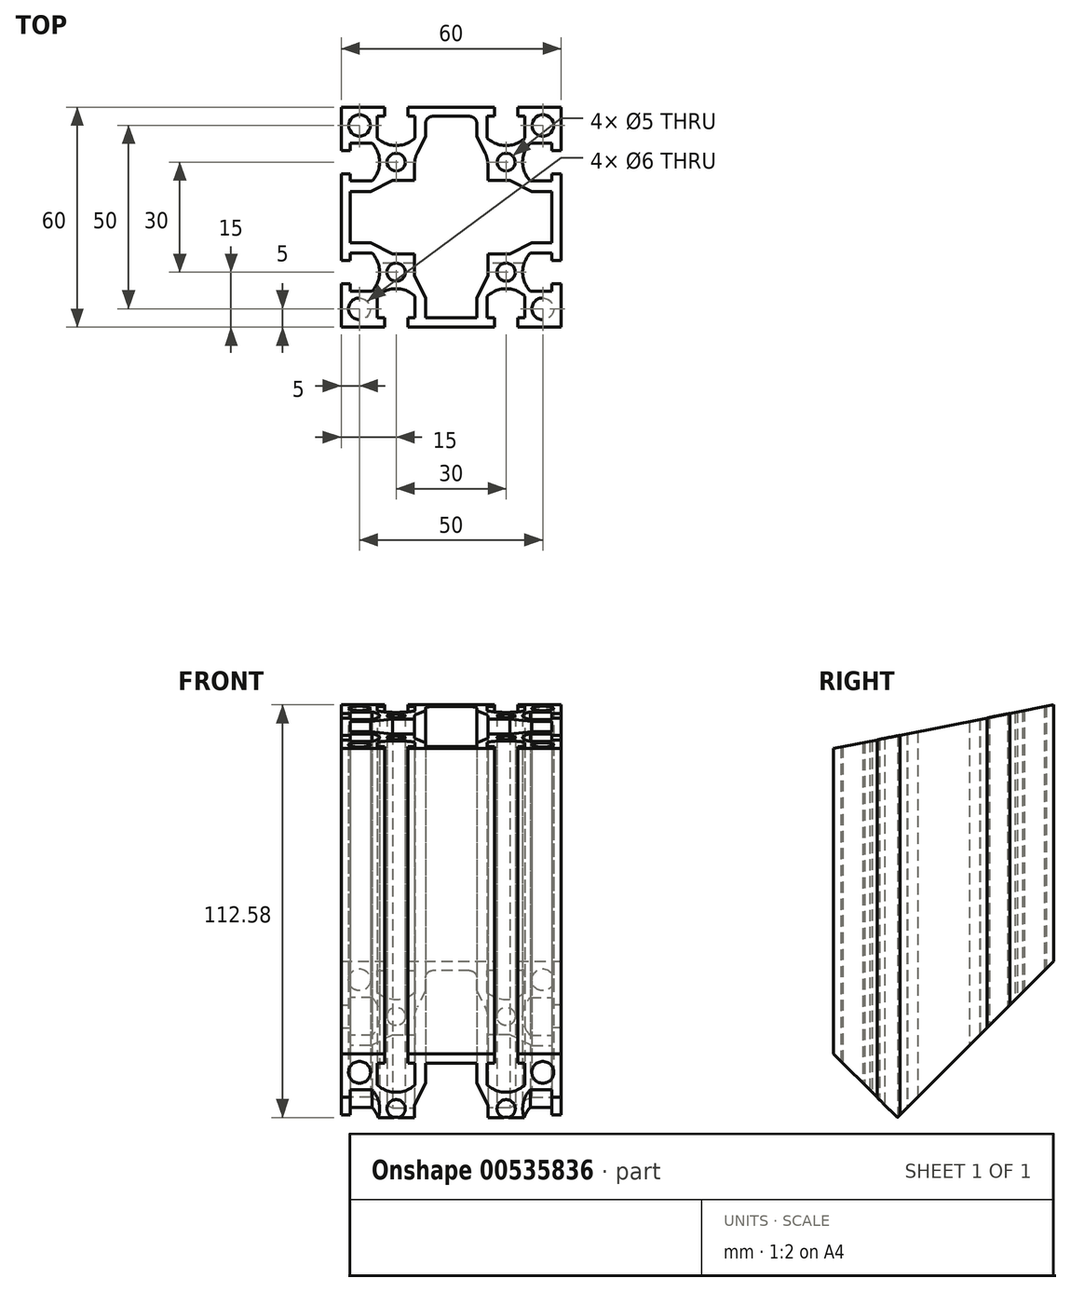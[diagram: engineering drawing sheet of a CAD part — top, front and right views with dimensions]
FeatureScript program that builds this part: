
annotation { "Feature Type Name" : "Feature", "Feature Type Description" : "" }
export const myFeature = defineFeature(function(context is Context, id is Id, definition is map)
    precondition{}
    {
        {
            var Q0;
            Q0=qCreatedBy(makeId("Top.planeOp"),FACE);
            var sketch = newSketch(context, id + "F0", { "sketchPlane" : qUnion([Q0])});
            skLineSegment(sketch, "E0.bottom", {"start": v(30, -30) * mm, "end": v(-30, -30) * mm});
            skLineSegment(sketch, "E0.top", {"start": v(30, 30) * mm, "end": v(-30, 30) * mm});
            skLineSegment(sketch, "E0.left", {"start": v(30, -30) * mm, "end": v(30, 30) * mm});
            skLineSegment(sketch, "E0.right", {"start": v(-30, -30) * mm, "end": v(-30, 30) * mm});
            skPoint(sketch, "E0.middle", {"position": v(0, 0) * mm});
            skLineSegment(sketch, "E1.top", {"start": v(-11.85, 30) * mm, "end": v(-18.15, 30) * mm});
            skLineSegment(sketch, "E1.left", {"start": v(-11.85, 27.5) * mm, "end": v(-11.85, 30) * mm});
            skLineSegment(sketch, "E1.right", {"start": v(-18.15, 27.5) * mm, "end": v(-18.15, 30) * mm});
            skPoint(sketch, "E1.middle", {"position": v(-15, 28.75) * mm});
            skLineSegment(sketch, "E2.bottom", {"start": v(-9.85, 27.5) * mm, "end": v(-11.85, 27.5) * mm});
            skLineSegment(sketch, "E2.left", {"start": v(-9.85, 27.5) * mm, "end": v(-9.85, 21.55) * mm});
            skLineSegment(sketch, "E2.right", {"start": v(-20.15, 27.5) * mm, "end": v(-20.15, 21.55) * mm});
            skPoint(sketch, "E2.middle", {"position": v(-15, 24.52) * mm});
            skArc(sketch, "E3", {"start": v(-20.15, 21.55) * mm, "mid": v(-15, 19.5) * mm, "end": v(-9.85, 21.55) * mm});
            skPoint(sketch, "E4.MirrorP", {"position": v(15, 24.52) * mm});
            skPoint(sketch, "E5.MirrorP", {"position": v(15, 28.75) * mm});
            skLineSegment(sketch, "E6.MirrorCS", {"start": v(11.85, 27.5) * mm, "end": v(11.85, 30) * mm});
            skLineSegment(sketch, "E7.MirrorCS", {"start": v(18.15, 27.5) * mm, "end": v(18.15, 30) * mm});
            skLineSegment(sketch, "E8.MirrorCS", {"start": v(9.85, 27.5) * mm, "end": v(11.85, 27.5) * mm});
            skLineSegment(sketch, "E9.MirrorCS", {"start": v(9.85, 27.5) * mm, "end": v(9.85, 21.55) * mm});
            skArc(sketch, "E10.MirrorCS", {"start": v(20.15, 21.55) * mm, "mid": v(15, 19.5) * mm, "end": v(9.85, 21.55) * mm});
            skLineSegment(sketch, "E11.MirrorCS", {"start": v(20.15, 27.5) * mm, "end": v(20.15, 21.55) * mm});
            skLineSegment(sketch, "E12.MirrorCS", {"start": v(11.85, 30) * mm, "end": v(18.15, 30) * mm});
            skLineSegment(sketch, "E13.1.0", {"start": v(27.5, 20.15) * mm, "end": v(21.55, 20.15) * mm});
            skLineSegment(sketch, "E13.1.1", {"start": v(27.5, 9.85) * mm, "end": v(21.55, 9.85) * mm});
            skArc(sketch, "E13.1.2", {"start": v(21.55, 20.15) * mm, "mid": v(19.5, 15) * mm, "end": v(21.55, 9.85) * mm});
            skLineSegment(sketch, "E13.1.3", {"start": v(27.5, -9.85) * mm, "end": v(21.55, -9.85) * mm});
            skLineSegment(sketch, "E13.1.4", {"start": v(27.5, -20.15) * mm, "end": v(21.55, -20.15) * mm});
            skPoint(sketch, "E13.1.5", {"position": v(28.75, 15) * mm});
            skPoint(sketch, "E13.1.6", {"position": v(28.75, -15) * mm});
            skArc(sketch, "E13.1.7", {"start": v(21.55, -20.15) * mm, "mid": v(19.5, -15) * mm, "end": v(21.55, -9.85) * mm});
            skPoint(sketch, "E13.1.8", {"position": v(24.52, -15) * mm});
            skPoint(sketch, "E13.1.9", {"position": v(24.52, 15) * mm});
            skLineSegment(sketch, "E13.1.10", {"start": v(27.5, 9.85) * mm, "end": v(27.5, 20.15) * mm});
            skLineSegment(sketch, "E13.1.11", {"start": v(27.5, -11.85) * mm, "end": v(27.5, -18.15) * mm});
            skLineSegment(sketch, "E13.1.12", {"start": v(30, 11.85) * mm, "end": v(30, 18.15) * mm});
            skLineSegment(sketch, "E13.1.13", {"start": v(30, -11.85) * mm, "end": v(30, -18.15) * mm});
            skLineSegment(sketch, "E13.1.14", {"start": v(27.5, 18.15) * mm, "end": v(30, 18.15) * mm});
            skLineSegment(sketch, "E13.1.15", {"start": v(27.5, 11.85) * mm, "end": v(30, 11.85) * mm});
            skLineSegment(sketch, "E13.1.16", {"start": v(27.5, 11.85) * mm, "end": v(27.5, 18.15) * mm});
            skLineSegment(sketch, "E13.1.17", {"start": v(27.5, -9.85) * mm, "end": v(27.5, -20.15) * mm});
            skLineSegment(sketch, "E13.1.18", {"start": v(27.5, -18.15) * mm, "end": v(30, -18.15) * mm});
            skLineSegment(sketch, "E13.1.19", {"start": v(27.5, -11.85) * mm, "end": v(30, -11.85) * mm});
            skLineSegment(sketch, "E13.2.0", {"start": v(20.15, -27.5) * mm, "end": v(20.15, -21.55) * mm});
            skLineSegment(sketch, "E13.2.1", {"start": v(9.85, -27.5) * mm, "end": v(9.85, -21.55) * mm});
            skArc(sketch, "E13.2.2", {"start": v(20.15, -21.55) * mm, "mid": v(15, -19.5) * mm, "end": v(9.85, -21.55) * mm});
            skLineSegment(sketch, "E13.2.3", {"start": v(-9.85, -27.5) * mm, "end": v(-9.85, -21.55) * mm});
            skLineSegment(sketch, "E13.2.4", {"start": v(-20.15, -27.5) * mm, "end": v(-20.15, -21.55) * mm});
            skPoint(sketch, "E13.2.5", {"position": v(15, -28.75) * mm});
            skPoint(sketch, "E13.2.6", {"position": v(-15, -28.75) * mm});
            skArc(sketch, "E13.2.7", {"start": v(-20.15, -21.55) * mm, "mid": v(-15, -19.5) * mm, "end": v(-9.85, -21.55) * mm});
            skPoint(sketch, "E13.2.8", {"position": v(-15, -24.52) * mm});
            skPoint(sketch, "E13.2.9", {"position": v(15, -24.52) * mm});
            skLineSegment(sketch, "E13.2.10", {"start": v(9.85, -27.5) * mm, "end": v(20.15, -27.5) * mm});
            skLineSegment(sketch, "E13.2.11", {"start": v(-11.85, -27.5) * mm, "end": v(-18.15, -27.5) * mm});
            skLineSegment(sketch, "E13.2.12", {"start": v(11.85, -30) * mm, "end": v(18.15, -30) * mm});
            skLineSegment(sketch, "E13.2.13", {"start": v(-11.85, -30) * mm, "end": v(-18.15, -30) * mm});
            skLineSegment(sketch, "E13.2.14", {"start": v(18.15, -27.5) * mm, "end": v(18.15, -30) * mm});
            skLineSegment(sketch, "E13.2.15", {"start": v(11.85, -27.5) * mm, "end": v(11.85, -30) * mm});
            skLineSegment(sketch, "E13.2.16", {"start": v(11.85, -27.5) * mm, "end": v(18.15, -27.5) * mm});
            skLineSegment(sketch, "E13.2.17", {"start": v(-9.85, -27.5) * mm, "end": v(-20.15, -27.5) * mm});
            skLineSegment(sketch, "E13.2.18", {"start": v(-18.15, -27.5) * mm, "end": v(-18.15, -30) * mm});
            skLineSegment(sketch, "E13.2.19", {"start": v(-11.85, -27.5) * mm, "end": v(-11.85, -30) * mm});
            skLineSegment(sketch, "E13.3.0", {"start": v(-27.5, -20.15) * mm, "end": v(-21.55, -20.15) * mm});
            skLineSegment(sketch, "E13.3.1", {"start": v(-27.5, -9.85) * mm, "end": v(-21.55, -9.85) * mm});
            skArc(sketch, "E13.3.2", {"start": v(-21.55, -20.15) * mm, "mid": v(-19.5, -15) * mm, "end": v(-21.55, -9.85) * mm});
            skLineSegment(sketch, "E13.3.3", {"start": v(-27.5, 9.85) * mm, "end": v(-21.55, 9.85) * mm});
            skLineSegment(sketch, "E13.3.4", {"start": v(-27.5, 20.15) * mm, "end": v(-21.55, 20.15) * mm});
            skPoint(sketch, "E13.3.5", {"position": v(-28.75, -15) * mm});
            skPoint(sketch, "E13.3.6", {"position": v(-28.75, 15) * mm});
            skArc(sketch, "E13.3.7", {"start": v(-21.55, 20.15) * mm, "mid": v(-19.5, 15) * mm, "end": v(-21.55, 9.85) * mm});
            skPoint(sketch, "E13.3.8", {"position": v(-24.52, 15) * mm});
            skPoint(sketch, "E13.3.9", {"position": v(-24.52, -15) * mm});
            skLineSegment(sketch, "E13.3.10", {"start": v(-27.5, -9.85) * mm, "end": v(-27.5, -20.15) * mm});
            skLineSegment(sketch, "E13.3.11", {"start": v(-27.5, 11.85) * mm, "end": v(-27.5, 18.15) * mm});
            skLineSegment(sketch, "E13.3.12", {"start": v(-30, -11.85) * mm, "end": v(-30, -18.15) * mm});
            skLineSegment(sketch, "E13.3.13", {"start": v(-30, 11.85) * mm, "end": v(-30, 18.15) * mm});
            skLineSegment(sketch, "E13.3.14", {"start": v(-27.5, -18.15) * mm, "end": v(-30, -18.15) * mm});
            skLineSegment(sketch, "E13.3.15", {"start": v(-27.5, -11.85) * mm, "end": v(-30, -11.85) * mm});
            skLineSegment(sketch, "E13.3.16", {"start": v(-27.5, -11.85) * mm, "end": v(-27.5, -18.15) * mm});
            skLineSegment(sketch, "E13.3.17", {"start": v(-27.5, 9.85) * mm, "end": v(-27.5, 20.15) * mm});
            skLineSegment(sketch, "E13.3.18", {"start": v(-27.5, 18.15) * mm, "end": v(-30, 18.15) * mm});
            skLineSegment(sketch, "E13.3.19", {"start": v(-27.5, 11.85) * mm, "end": v(-30, 11.85) * mm});
            skLineSegment(sketch, "E13.anchor1", {"start": v(0, 0) * mm, "end": v(-20.15, 21.55) * mm, "construction": true});
            skLineSegment(sketch, "E13.anchor2", {"start": v(0, 0) * mm, "end": v(-21.55, -20.15) * mm, "construction": true});
            skLineSegment(sketch, "E14.trimOffspring", {"start": v(-18.15, 27.5) * mm, "end": v(-20.15, 27.5) * mm});
            skLineSegment(sketch, "E15.trimOffspring", {"start": v(18.15, 27.5) * mm, "end": v(20.15, 27.5) * mm});
            skCircle(sketch, "E16", {"center": v(-15, 15) * mm, "radius": 2.5 * mm});
            skCircle(sketch, "E17", {"center": v(-25, 25) * mm, "radius": 3 * mm});
            skCircle(sketch, "E18.MirrorC", {"center": v(25, 25) * mm, "radius": 3 * mm});
            skCircle(sketch, "E19.MirrorC", {"center": v(25, -25) * mm, "radius": 3 * mm});
            skCircle(sketch, "E20.MirrorC", {"center": v(-25, -25) * mm, "radius": 3 * mm});
            skCircle(sketch, "E21.MirrorC", {"center": v(15, 15) * mm, "radius": 2.5 * mm});
            skCircle(sketch, "E22.MirrorC", {"center": v(15, -15) * mm, "radius": 2.5 * mm});
            skCircle(sketch, "E23.MirrorC", {"center": v(-15, -15) * mm, "radius": 2.5 * mm});
            skLineSegment(sketch, "E24", {"start": v(-7, 27.5) * mm, "end": v(0, 27.5) * mm});
            skLineSegment(sketch, "E25", {"start": v(-7, 27.5) * mm, "end": v(-7, 22) * mm});
            skLineSegment(sketch, "E26", {"start": v(-10, 10) * mm, "end": v(-10, 16) * mm});
            skLineSegment(sketch, "E27", {"start": v(-10, 16) * mm, "end": v(-7, 22) * mm});
            skLineSegment(sketch, "E28.MirrorCS", {"start": v(10, 10) * mm, "end": v(10, 16) * mm});
            skLineSegment(sketch, "E29.MirrorCS", {"start": v(10, 16) * mm, "end": v(7, 22) * mm});
            skLineSegment(sketch, "E30.MirrorCS", {"start": v(7, 27.5) * mm, "end": v(0, 27.5) * mm});
            skLineSegment(sketch, "E31.MirrorCS", {"start": v(7, 27.5) * mm, "end": v(7, 22) * mm});
            skLineSegment(sketch, "E32.1.0", {"start": v(-10, -10) * mm, "end": v(-16, -10) * mm});
            skLineSegment(sketch, "E32.1.1", {"start": v(-16, -10) * mm, "end": v(-22, -7) * mm});
            skLineSegment(sketch, "E32.1.2", {"start": v(-27.5, -7) * mm, "end": v(-22, -7) * mm});
            skLineSegment(sketch, "E32.1.3", {"start": v(-27.5, -7) * mm, "end": v(-27.5, 0) * mm});
            skLineSegment(sketch, "E32.1.4", {"start": v(-27.5, 7) * mm, "end": v(-27.5, 0) * mm});
            skLineSegment(sketch, "E32.1.5", {"start": v(-27.5, 7) * mm, "end": v(-22, 7) * mm});
            skLineSegment(sketch, "E32.1.6", {"start": v(-16, 10) * mm, "end": v(-22, 7) * mm});
            skLineSegment(sketch, "E32.1.7", {"start": v(-10, 10) * mm, "end": v(-16, 10) * mm});
            skLineSegment(sketch, "E32.2.0", {"start": v(10, -10) * mm, "end": v(10, -16) * mm});
            skLineSegment(sketch, "E32.2.1", {"start": v(10, -16) * mm, "end": v(7, -22) * mm});
            skLineSegment(sketch, "E32.2.2", {"start": v(7, -27.5) * mm, "end": v(7, -22) * mm});
            skLineSegment(sketch, "E32.2.3", {"start": v(7, -27.5) * mm, "end": v(0, -27.5) * mm});
            skLineSegment(sketch, "E32.2.4", {"start": v(-7, -27.5) * mm, "end": v(0, -27.5) * mm});
            skLineSegment(sketch, "E32.2.5", {"start": v(-7, -27.5) * mm, "end": v(-7, -22) * mm});
            skLineSegment(sketch, "E32.2.6", {"start": v(-10, -16) * mm, "end": v(-7, -22) * mm});
            skLineSegment(sketch, "E32.2.7", {"start": v(-10, -10) * mm, "end": v(-10, -16) * mm});
            skLineSegment(sketch, "E32.3.0", {"start": v(10, 10) * mm, "end": v(16, 10) * mm});
            skLineSegment(sketch, "E32.3.1", {"start": v(16, 10) * mm, "end": v(22, 7) * mm});
            skLineSegment(sketch, "E32.3.2", {"start": v(27.5, 7) * mm, "end": v(22, 7) * mm});
            skLineSegment(sketch, "E32.3.3", {"start": v(27.5, 7) * mm, "end": v(27.5, 0) * mm});
            skLineSegment(sketch, "E32.3.4", {"start": v(27.5, -7) * mm, "end": v(27.5, 0) * mm});
            skLineSegment(sketch, "E32.3.5", {"start": v(27.5, -7) * mm, "end": v(22, -7) * mm});
            skLineSegment(sketch, "E32.3.6", {"start": v(16, -10) * mm, "end": v(22, -7) * mm});
            skLineSegment(sketch, "E32.3.7", {"start": v(10, -10) * mm, "end": v(16, -10) * mm});
            skSolve(sketch);
        }
        {
            var Q0;
            {var subQ30=sQuery(id+"F0.wireOp",EDGE,"E1.left");Q0=makeQuery(id+"F0.imprint","IMPRINT",FACE,{"disambiguationData":[TD([[makeQuery(id+"F0.imprint","IMPRINT",EDGE,{"derivedFrom":subQ30}),-1.0]])]});}
            extrude(context, id + "F1", {"entities" : qUnion([Q0]), "depth" : 130 * mm, "offsetDistance" : 25 * mm});
        }
        {
            var Q0;
            Q0=makeQuery(id+"F1.opExtrude","SWEPT_EDGE",EDGE,{"disambiguationData":[OSD([sQuery(id+"F0.wireOp",EDGE,"E24"),sQuery(id+"F0.wireOp",EDGE,"E25")])]});
            var Q1;
            Q1=makeQuery(id+"F1.opExtrude","SWEPT_EDGE",EDGE,{"disambiguationData":[OSD([sQuery(id+"F0.wireOp",EDGE,"E30.MirrorCS"),sQuery(id+"F0.wireOp",EDGE,"E31.MirrorCS")])]});
            var Q2;
            Q2=makeQuery(id+"F1.opExtrude","SWEPT_EDGE",EDGE,{"disambiguationData":[OSD([sQuery(id+"F0.wireOp",EDGE,"840db5bc-c403-45cd-90c7-254e62d9e8c5.3.2"),sQuery(id+"F0.wireOp",EDGE,"840db5bc-c403-45cd-90c7-254e62d9e8c5.3.3")])]});
            var Q3;
            Q3=makeQuery(id+"F1.opExtrude","SWEPT_EDGE",EDGE,{"disambiguationData":[OSD([sQuery(id+"F0.wireOp",EDGE,"840db5bc-c403-45cd-90c7-254e62d9e8c5.3.4"),sQuery(id+"F0.wireOp",EDGE,"840db5bc-c403-45cd-90c7-254e62d9e8c5.3.5")])]});
            var Q4;
            Q4=makeQuery(id+"F1.opExtrude","SWEPT_EDGE",EDGE,{"disambiguationData":[OSD([sQuery(id+"F0.wireOp",EDGE,"840db5bc-c403-45cd-90c7-254e62d9e8c5.1.4"),sQuery(id+"F0.wireOp",EDGE,"840db5bc-c403-45cd-90c7-254e62d9e8c5.1.5")])]});
            var Q5;
            Q5=makeQuery(id+"F1.opExtrude","SWEPT_EDGE",EDGE,{"disambiguationData":[OSD([sQuery(id+"F0.wireOp",EDGE,"840db5bc-c403-45cd-90c7-254e62d9e8c5.1.2"),sQuery(id+"F0.wireOp",EDGE,"840db5bc-c403-45cd-90c7-254e62d9e8c5.1.3")])]});
            var Q6;
            Q6=makeQuery(id+"F1.opExtrude","SWEPT_EDGE",EDGE,{"disambiguationData":[OSD([sQuery(id+"F0.wireOp",EDGE,"840db5bc-c403-45cd-90c7-254e62d9e8c5.2.2"),sQuery(id+"F0.wireOp",EDGE,"840db5bc-c403-45cd-90c7-254e62d9e8c5.2.3")])]});
            var Q7;
            Q7=makeQuery(id+"F1.opExtrude","SWEPT_EDGE",EDGE,{"disambiguationData":[OSD([sQuery(id+"F0.wireOp",EDGE,"840db5bc-c403-45cd-90c7-254e62d9e8c5.2.4"),sQuery(id+"F0.wireOp",EDGE,"840db5bc-c403-45cd-90c7-254e62d9e8c5.2.5")])]});
            fillet(context, id + "F2", {"entities" : qUnion([Q0, Q1, Q2, Q3, Q4, Q5, Q6, Q7]), "radius" : 2 * mm, "tangentPropagation" : true, "allowEdgeOverflow" : false});
        }
        {
            var Q0;
            Q0=makeQuery(id+"F1.opExtrude","SWEPT_EDGE",EDGE,{"disambiguationData":[OSD([sQuery(id+"F0.wireOp",EDGE,"E26"),sQuery(id+"F0.wireOp",EDGE,"E27")])]});
            var Q1;
            Q1=makeQuery(id+"F1.opExtrude","SWEPT_EDGE",EDGE,{"disambiguationData":[OSD([sQuery(id+"F0.wireOp",EDGE,"E28.MirrorCS"),sQuery(id+"F0.wireOp",EDGE,"E29.MirrorCS")])]});
            var Q2;
            Q2=makeQuery(id+"F1.opExtrude","SWEPT_EDGE",EDGE,{"disambiguationData":[OSD([sQuery(id+"F0.wireOp",EDGE,"840db5bc-c403-45cd-90c7-254e62d9e8c5.3.0"),sQuery(id+"F0.wireOp",EDGE,"840db5bc-c403-45cd-90c7-254e62d9e8c5.3.1")])]});
            var Q3;
            Q3=makeQuery(id+"F1.opExtrude","SWEPT_EDGE",EDGE,{"disambiguationData":[OSD([sQuery(id+"F0.wireOp",EDGE,"840db5bc-c403-45cd-90c7-254e62d9e8c5.1.6"),sQuery(id+"F0.wireOp",EDGE,"840db5bc-c403-45cd-90c7-254e62d9e8c5.1.7")])]});
            var Q4;
            Q4=makeQuery(id+"F1.opExtrude","SWEPT_EDGE",EDGE,{"disambiguationData":[OSD([sQuery(id+"F0.wireOp",EDGE,"840db5bc-c403-45cd-90c7-254e62d9e8c5.1.0"),sQuery(id+"F0.wireOp",EDGE,"840db5bc-c403-45cd-90c7-254e62d9e8c5.1.1")])]});
            var Q5;
            Q5=makeQuery(id+"F1.opExtrude","SWEPT_EDGE",EDGE,{"disambiguationData":[OSD([sQuery(id+"F0.wireOp",EDGE,"840db5bc-c403-45cd-90c7-254e62d9e8c5.3.6"),sQuery(id+"F0.wireOp",EDGE,"840db5bc-c403-45cd-90c7-254e62d9e8c5.3.7")])]});
            var Q6;
            Q6=makeQuery(id+"F1.opExtrude","SWEPT_EDGE",EDGE,{"disambiguationData":[OSD([sQuery(id+"F0.wireOp",EDGE,"840db5bc-c403-45cd-90c7-254e62d9e8c5.2.0"),sQuery(id+"F0.wireOp",EDGE,"840db5bc-c403-45cd-90c7-254e62d9e8c5.2.1")])]});
            var Q7;
            Q7=makeQuery(id+"F1.opExtrude","SWEPT_EDGE",EDGE,{"disambiguationData":[OSD([sQuery(id+"F0.wireOp",EDGE,"840db5bc-c403-45cd-90c7-254e62d9e8c5.2.6"),sQuery(id+"F0.wireOp",EDGE,"840db5bc-c403-45cd-90c7-254e62d9e8c5.2.7")])]});
            fillet(context, id + "F3", {"entities" : qUnion([Q0, Q1, Q2, Q3, Q4, Q5, Q6, Q7]), "radius" : 7 * mm, "tangentPropagation" : true, "allowEdgeOverflow" : false});
        }
        {
            var Q0;
            {var subQ0=sQuery(id+"F0.wireOp",EDGE,"E0.bottom");Q0=makeQuery(id+"F1.opExtrude","SWEPT_FACE",FACE,{"disambiguationData":[OSD([subQ0]),TDD([makeQuery(id+"F0.imprint","IMPRINT",EDGE,{"disambiguationData":[TD([[makeQuery(id+"F0.imprint","INTERSECT",VERTEX,{"derivedFrom":[subQ0,sQuery(id+"F0.wireOp",EDGE,"E13.2.12"),sQuery(id+"F0.wireOp",EDGE,"E13.2.15")]}),-1.0]])],"derivedFrom":subQ0})])]});}
            var sketch = newSketch(context, id + "F4", { "sketchPlane" : qUnion([Q0])});
            skLineSegment(sketch, "E33.0", {"start": v(-18.15, 130) * mm, "end": v(-30, 130) * mm});
            skLineSegment(sketch, "E33.1", {"start": v(30, 130) * mm, "end": v(30, 0) * mm});
            skLineSegment(sketch, "E34", {"start": v(-30, 130) * mm, "end": v(30, 130) * mm});
            skLineSegment(sketch, "E35", {"start": v(30, 70) * mm, "end": v(-30, 130) * mm});
            skLineSegment(sketch, "E36.0", {"start": v(-18.15, 0) * mm, "end": v(-30, 0) * mm});
            skLineSegment(sketch, "E37", {"start": v(-30, 0) * mm, "end": v(30, 0) * mm});
            skLineSegment(sketch, "E38", {"start": v(30, 60) * mm, "end": v(-30, 0) * mm});
            skSolve(sketch);
        }
        {
            var Q0;
            Q0=qCreatedBy(makeId("Right.planeOp"),FACE);
            var sketch = newSketch(context, id + "F5", { "sketchPlane" : qUnion([Q0])});
            skLineSegment(sketch, "E39.bottom", {"start": v(64.9, 94.9) * mm, "end": v(-30, 0) * mm});
            skLineSegment(sketch, "E39.top", {"start": v(115.26, 44.52) * mm, "end": v(20.37, -50.37) * mm});
            skLineSegment(sketch, "E39.left", {"start": v(64.9, 94.9) * mm, "end": v(115.26, 44.52) * mm});
            skLineSegment(sketch, "E39.right", {"start": v(-30, 0) * mm, "end": v(20.37, -50.37) * mm});
            skLineSegment(sketch, "E40.bottom", {"start": v(10.77, 226.68) * mm, "end": v(-148.72, 194.96) * mm});
            skLineSegment(sketch, "E40.top", {"start": v(30, 130) * mm, "end": v(-129.5, 98.27) * mm});
            skLineSegment(sketch, "E40.left", {"start": v(10.77, 226.68) * mm, "end": v(30, 130) * mm});
            skLineSegment(sketch, "E40.right", {"start": v(-148.72, 194.96) * mm, "end": v(-129.5, 98.27) * mm});
            skSolve(sketch);
        }
        {
            var Q0;
            Q0 = qSketchRegion(id + "F5", true);
            extrude(context, id + "F6", {"entities" : qUnion([Q0]), "operationType" : NewBodyOperationType.REMOVE, "depth" : 30 * mm, "offsetDistance" : 25 * mm, "hasSecondDirection" : true, "secondDirectionOppositeDirection" : true, "secondDirectionDepth" : 30 * mm});
        }
        {
            var Q0;
            Q0=qCreatedBy(makeId("Right.planeOp"),FACE);
            var sketch = newSketch(context, id + "F7", { "sketchPlane" : qUnion([Q0])});
            skLineSegment(sketch, "E41", {"start": v(-3.9, 8.78) * mm, "end": v(-35.01, 39.7) * mm});
            skLineSegment(sketch, "E42", {"start": v(-35.01, 39.7) * mm, "end": v(-51.91, -8.63) * mm});
            skLineSegment(sketch, "E43", {"start": v(-51.91, -8.63) * mm, "end": v(-17.65, -8.63) * mm});
            skLineSegment(sketch, "E44", {"start": v(-17.65, -8.63) * mm, "end": v(-3.9, 8.78) * mm});
            skSolve(sketch);
        }
        {
            var Q0;
            Q0 = qSketchRegion(id + "F7", true);
            extrude(context, id + "F8", {"entities" : qUnion([Q0]), "operationType" : NewBodyOperationType.REMOVE, "depth" : 30 * mm, "offsetDistance" : 25 * mm, "hasSecondDirection" : true, "secondDirectionOppositeDirection" : true, "secondDirectionDepth" : 30 * mm});
        }
    });
